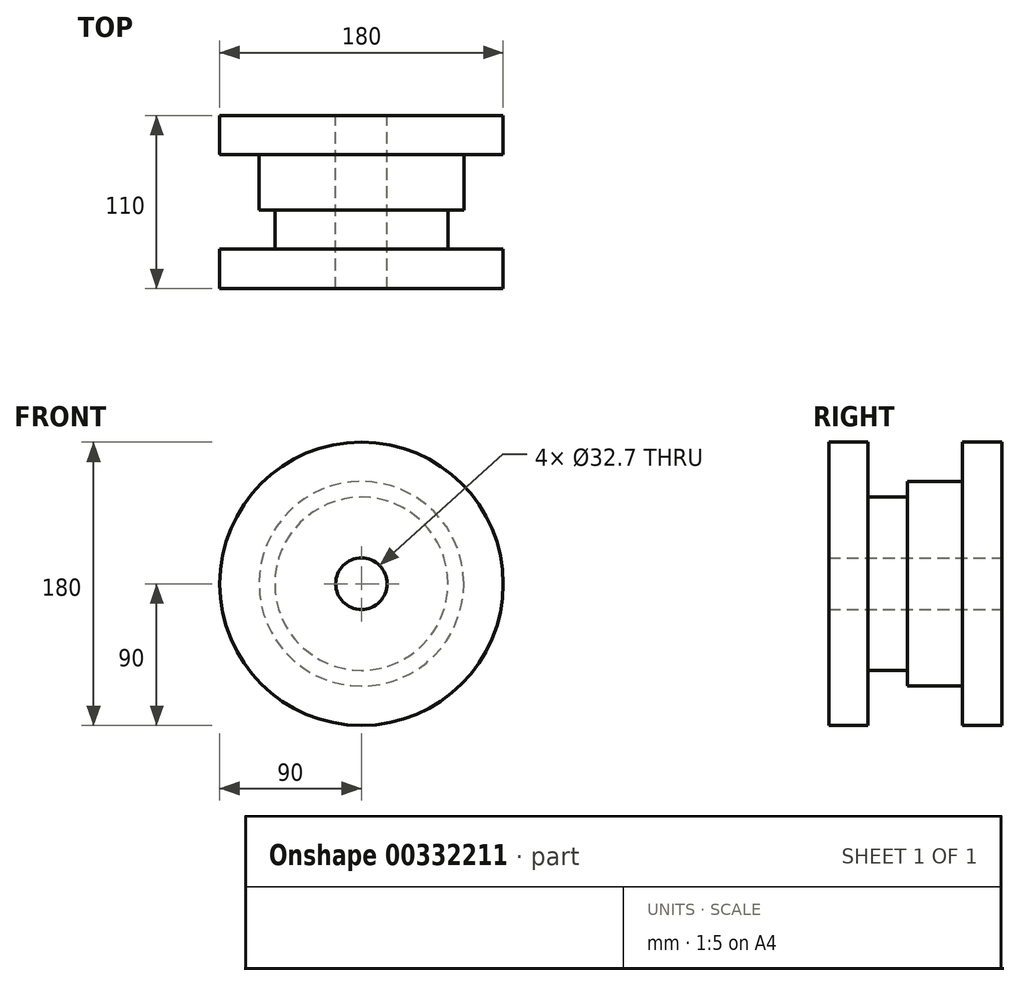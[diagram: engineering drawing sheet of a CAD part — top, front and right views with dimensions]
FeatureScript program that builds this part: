
annotation { "Feature Type Name" : "Feature", "Feature Type Description" : "" }
export const myFeature = defineFeature(function(context is Context, id is Id, definition is map)
    precondition{}
    {
        {
            var Q0;
            Q0=qCreatedBy(makeId("Top.planeOp"),FACE);
            var sketch = newSketch(context, id + "F0", { "sketchPlane" : qUnion([Q0])});
            skLineSegment(sketch, "E0", {"start": v(0, 0) * mm, "end": v(90, 0) * mm});
            skLineSegment(sketch, "E1", {"start": v(90, 0) * mm, "end": v(90, 25) * mm});
            skLineSegment(sketch, "E2", {"start": v(90, 25) * mm, "end": v(55, 25) * mm});
            skLineSegment(sketch, "E3", {"start": v(55, 25) * mm, "end": v(55, 50) * mm});
            skLineSegment(sketch, "E4", {"start": v(55, 50) * mm, "end": v(65, 50) * mm});
            skLineSegment(sketch, "E5", {"start": v(65, 50) * mm, "end": v(65, 85) * mm});
            skLineSegment(sketch, "E6", {"start": v(65, 85) * mm, "end": v(90, 85) * mm});
            skLineSegment(sketch, "E7", {"start": v(90, 85) * mm, "end": v(90, 110) * mm});
            skLineSegment(sketch, "E8", {"start": v(90, 110) * mm, "end": v(0, 110) * mm});
            skLineSegment(sketch, "E9", {"start": v(0, 110) * mm, "end": v(0, 0) * mm});
            skLineSegment(sketch, "E10", {"start": v(16.35, 110) * mm, "end": v(16.35, 0) * mm});
            skSolve(sketch);
        }
        {
            var Q0;
            {var subQ0=sQuery(id+"F0.wireOp",EDGE,"E1");Q0=makeQuery(id+"F0.imprint","IMPRINT",FACE,{"disambiguationData":[TD([[makeQuery(id+"F0.imprint","IMPRINT",EDGE,{"derivedFrom":subQ0}),1.0]])]});}
            var Q1;
            Q1=sQuery(id+"F0.wireOp",EDGE,"E9");
            revolve(context, id + "F1", {"entities" : qUnion([Q0]), "axis" : qUnion([Q1]), "revolveType" : RevolveType.FULL});
        }
        {
            var Q0;
            Q0=makeQuery(id+"F1.opRevolve","SWEPT_BODY",BODY,{"disambiguationData":[OSD([sQuery(id+"F0.wireOp",EDGE,"E0"),sQuery(id+"F0.wireOp",EDGE,"E1"),sQuery(id+"F0.wireOp",EDGE,"E2"),sQuery(id+"F0.wireOp",EDGE,"E3"),sQuery(id+"F0.wireOp",EDGE,"E4"),sQuery(id+"F0.wireOp",EDGE,"E5"),sQuery(id+"F0.wireOp",EDGE,"E6"),sQuery(id+"F0.wireOp",EDGE,"E7"),sQuery(id+"F0.wireOp",EDGE,"E8"),sQuery(id+"F0.wireOp",EDGE,"E10")])]});
            var Q1;
            Q1=makeQuery(id+"F1.opRevolve","SWEPT_EDGE",EDGE,{"disambiguationData":[OSD([sQuery(id+"F0.wireOp",EDGE,"E8"),sQuery(id+"F0.wireOp",EDGE,"E10")])]});
            circularPattern(context, id + "F2", {"entities" : qUnion([Q0]), "axis" : qUnion([Q1]), "angle" : 360 * degree, "instanceCount" : 4, "equalSpace" : true});
        }
    });
